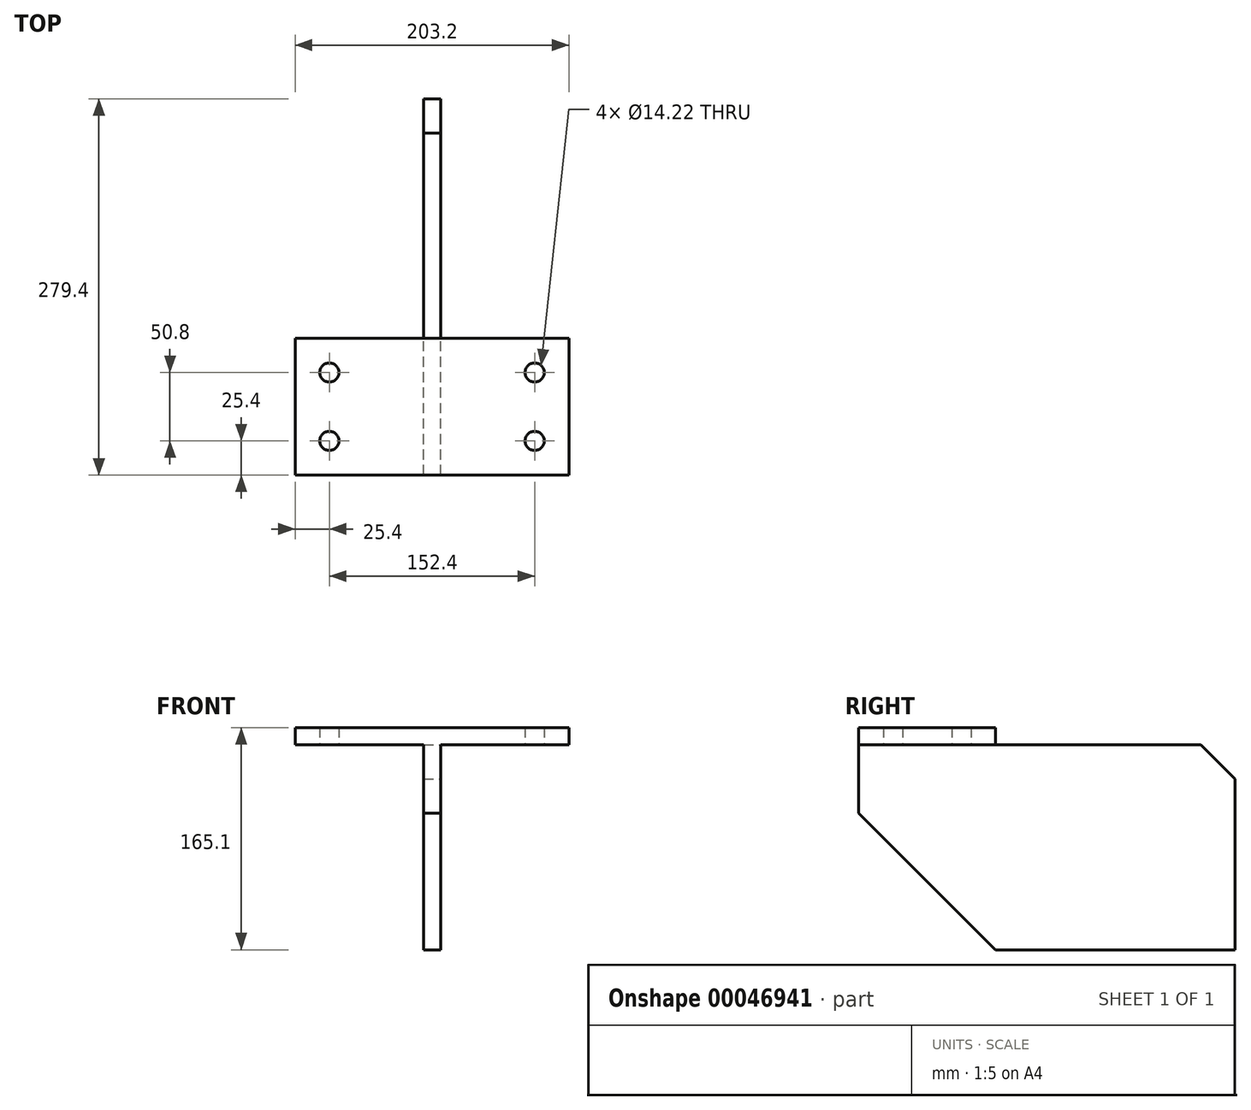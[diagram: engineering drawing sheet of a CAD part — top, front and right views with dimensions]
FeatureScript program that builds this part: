
annotation { "Feature Type Name" : "Feature", "Feature Type Description" : "" }
export const myFeature = defineFeature(function(context is Context, id is Id, definition is map)
    precondition{}
    {
        {
            var Q0;
            Q0=qCreatedBy(makeId("Top.planeOp"),FACE);
            var sketch = newSketch(context, id + "F0", { "sketchPlane" : qUnion([Q0])});
            skLineSegment(sketch, "E0.0", {"start": v(-101.6, 50.8) * mm, "end": v(-101.6, -50.8) * mm});
            skLineSegment(sketch, "E1.0", {"start": v(-101.6, -50.8) * mm, "end": v(101.6, -50.8) * mm});
            skCircle(sketch, "E2.0", {"center": v(-76.2, -25.4) * mm, "radius": 7.11 * mm});
            skCircle(sketch, "E3.0", {"center": v(-76.2, 25.4) * mm, "radius": 7.11 * mm});
            skLineSegment(sketch, "E4.0", {"start": v(-101.6, 50.8) * mm, "end": v(101.6, 50.8) * mm});
            skCircle(sketch, "E5.0", {"center": v(76.2, 25.4) * mm, "radius": 7.11 * mm});
            skCircle(sketch, "E6.0", {"center": v(76.2, -25.4) * mm, "radius": 7.11 * mm});
            skLineSegment(sketch, "E7.0", {"start": v(101.6, 50.8) * mm, "end": v(101.6, -50.8) * mm});
            skSolve(sketch);
        }
        {
            var Q0;
            Q0 = qSketchRegion(id + "F0", true);
            extrude(context, id + "F1", {"entities" : qUnion([Q0]), "depth" : 12.7 * mm});
        }
        {
            var Q0;
            Q0=makeQuery(id+"F1.opExtrude","CAP_FACE",FACE,{"disambiguationData":[OSD([sQuery(id+"F0.wireOp",EDGE,"E0.0"),sQuery(id+"F0.wireOp",EDGE,"E1.0"),sQuery(id+"F0.wireOp",EDGE,"E2.0"),sQuery(id+"F0.wireOp",EDGE,"E3.0"),sQuery(id+"F0.wireOp",EDGE,"E4.0"),sQuery(id+"F0.wireOp",EDGE,"E5.0"),sQuery(id+"F0.wireOp",EDGE,"E6.0"),sQuery(id+"F0.wireOp",EDGE,"E7.0")])],"isStart":true});
            var sketch = newSketch(context, id + "F2", { "sketchPlane" : qUnion([Q0])});
            skLineSegment(sketch, "E8.0", {"start": v(-101.6, 50.8) * mm, "end": v(101.6, 50.8) * mm, "construction": true});
            skLineSegment(sketch, "E9", {"start": v(0, 0) * mm, "end": v(0, 111.66) * mm, "construction": true});
            skPoint(sketch, "E9.endSnap0", {"position": v(0, 50.8) * mm});
            skLineSegment(sketch, "E10.0", {"start": v(-6.35, 0) * mm, "end": v(-6.35, 111.66) * mm, "construction": true});
            skLineSegment(sketch, "E11.bottom", {"start": v(-6.35, 50.8) * mm, "end": v(6.35, 50.8) * mm});
            skLineSegment(sketch, "E11.top", {"start": v(-6.35, -228.6) * mm, "end": v(6.35, -228.6) * mm});
            skLineSegment(sketch, "E11.left", {"start": v(-6.35, 50.8) * mm, "end": v(-6.35, -228.6) * mm});
            skLineSegment(sketch, "E11.right", {"start": v(6.35, 50.8) * mm, "end": v(6.35, -228.6) * mm});
            skSolve(sketch);
        }
        {
            var Q0;
            Q0 = qSketchRegion(id + "F2", true);
            extrude(context, id + "F3", {"entities" : qUnion([Q0]), "operationType" : NewBodyOperationType.ADD, "depth" : 152.4 * mm});
        }
        {
            var Q0;
            Q0=makeQuery(id+"F3.opExtrude","CAP_EDGE",EDGE,{"disambiguationData":[OSD([sQuery(id+"F2.wireOp",EDGE,"E11.bottom")])],"isStart":false});
            chamfer(context, id + "F4", {"entities" : qUnion([Q0]), "width" : 101.6 * mm, "tangentPropagation" : true});
        }
        {
            var Q0;
            Q0=makeQuery(id+"F3.opExtrude","CAP_EDGE",EDGE,{"disambiguationData":[OSD([sQuery(id+"F2.wireOp",EDGE,"E11.top")])],"isStart":true});
            chamfer(context, id + "F5", {"entities" : qUnion([Q0]), "width" : 25.4 * mm, "tangentPropagation" : true});
        }
    });
